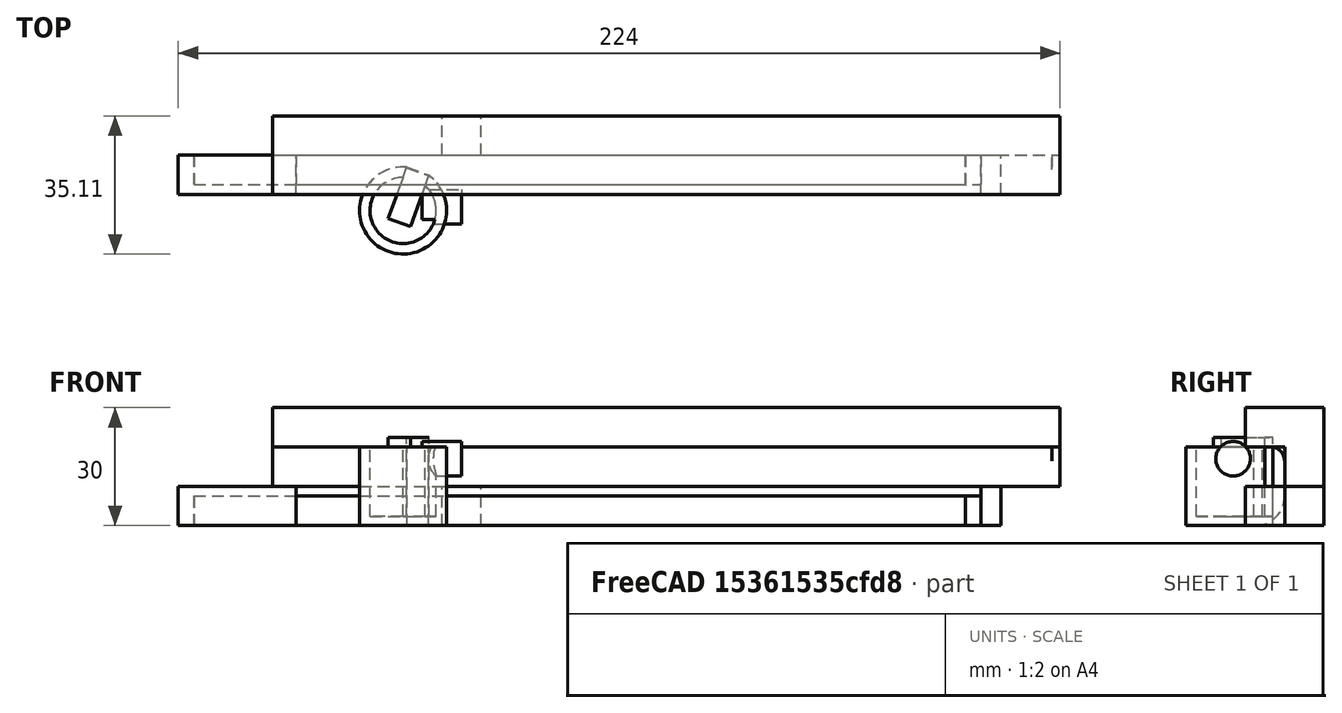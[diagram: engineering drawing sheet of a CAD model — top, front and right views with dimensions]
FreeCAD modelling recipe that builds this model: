
FCSTD DOCUMENT  (FreeCAD 0.19R0.19.2)
Label: v0_76
License: All rights reserved
LicenseURL: http://en.wikipedia.org/wiki/All_rights_reserved
objects: Part::Box×43, Part::Fillet×31, Part::MultiFuse×20, Part::Cut×13, Sketcher::SketchObject×11, Part::Extrusion×9, Part::Cylinder×6, App::MeasureDistance×5, Part::Revolution×1
note: 134 computed .brp shape members not serialized (recipe doc carries the construction recipe); baked Part::Feature solids carry a one-line shape summary decoded from their .brp

FEATURE [Sketcher::SketchObject] Sketch001
  FullyConstrained = true
  sketch-geometry (47):
    g0: Circle CenterX=-129.5 CenterY=-8 CenterZ=0 NormalX=0 NormalY=0 NormalZ=1 AngleXU=0 Radius=1
    g1: Circle CenterX=-129.5 CenterY=-3 CenterZ=0 NormalX=0 NormalY=0 NormalZ=1 AngleXU=0 Radius=1
    g2: Circle CenterX=-124.5 CenterY=-3 CenterZ=0 NormalX=0 NormalY=0 NormalZ=1 AngleXU=0 Radius=1
    g3: BSplineCurve PolesCount=3 KnotsCount=2 Degree=2 IsPeriodic=0
    g4: GeomPoint X=-129.5 Y=-8 Z=0
    g5: GeomPoint X=-124.5 Y=-3 Z=0
    g6: LineSegment StartX=18.6 StartY=-2.9 StartZ=0 EndX=23.6 EndY=-2.9 EndZ=0
    g7: ArcOfCircle CenterX=23.8 CenterY=-14.35 CenterZ=0 NormalX=0 NormalY=0 NormalZ=1 AngleXU=0 Radius=2.3 StartAngle=8e-16 EndAngle=1.5708
    g8: ArcOfCircle CenterX=23.8 CenterY=-18.1 CenterZ=0 NormalX=0 NormalY=0 NormalZ=1 AngleXU=0 Radius=2.3 StartAngle=4.71239 EndAngle=6.28319
    g9: LineSegment StartX=23.8 StartY=-20.4 StartZ=0 EndX=21.1 EndY=-20.4 EndZ=0
    g10: LineSegment StartX=21.1 StartY=-22.9 StartZ=0 EndX=21.1 EndY=-20.4 EndZ=0
    g11: LineSegment StartX=26.1 StartY=-14.35 StartZ=0 EndX=26.1 EndY=-18.1 EndZ=0
    g12: LineSegment StartX=18.6 StartY=-5.40742 StartZ=0 EndX=18.6 EndY=-2.9 EndZ=0
    g13: ArcOfCircle CenterX=18.8 CenterY=-8.1 CenterZ=0 NormalX=0 NormalY=0 NormalZ=1 AngleXU=0 Radius=2.7 StartAngle=1.64494 EndAngle=3.14159
    g14: ArcOfCircle CenterX=18.8 CenterY=-11.85 CenterZ=0 NormalX=0 NormalY=0 NormalZ=1 AngleXU=0 Radius=2.7 StartAngle=3.14159 EndAngle=4.71239
    g15: LineSegment StartX=16.1 StartY=-8.1 StartZ=0 EndX=16.1 EndY=-11.85 EndZ=0
    g16: LineSegment StartX=18.8 StartY=-14.55 StartZ=0 EndX=21.5 EndY=-14.55 EndZ=0
    g17: LineSegment StartX=21.5 StartY=-12.05 StartZ=0 EndX=21.5 EndY=-14.55 EndZ=0
    g18: LineSegment StartX=21.5 StartY=-12.05 StartZ=0 EndX=23.8 EndY=-12.05 EndZ=0
    g19: LineSegment StartX=16.1 StartY=-22.9 StartZ=0 EndX=21.1 EndY=-22.9 EndZ=0
    g20: LineSegment StartX=23.6 StartY=-2.9 StartZ=0 EndX=23.6 EndY=0 EndZ=0
    g21: LineSegment StartX=16.1 StartY=-22.9 StartZ=0 EndX=16.1 EndY=-26.2 EndZ=0
    g22: BSplineCurve PolesCount=3 KnotsCount=2 Degree=2 IsPeriodic=0
    g23: LineSegment StartX=2.6 StartY=-3 StartZ=0 EndX=-124.5 EndY=-3 EndZ=0
    g24: ArcOfCircle CenterX=-134.9 CenterY=-8.6 CenterZ=0 NormalX=0 NormalY=0 NormalZ=1 AngleXU=0 Radius=0.5 StartAngle=4.71238 EndAngle=6.28319
    g25: LineSegment StartX=-141.9 StartY=-9.1 StartZ=0 EndX=-134.9 EndY=-9.1 EndZ=0
    g26: LineSegment StartX=-141.9 StartY=-33.8 StartZ=0 EndX=-141.5 EndY=-33.8 EndZ=0
    g27: LineSegment StartX=-141.9 StartY=-9.1 StartZ=0 EndX=-141.9 EndY=-33.8 EndZ=0
    g28: LineSegment StartX=-134.4 StartY=-8.6 StartZ=0 EndX=-134.4 EndY=0 EndZ=0
    g29: LineSegment StartX=-134.4 StartY=0 StartZ=0 EndX=23.6 EndY=0 EndZ=0
    g30: LineSegment StartX=-133.5 StartY=-26.2 StartZ=0 EndX=16.1 EndY=-26.2 EndZ=0
    g31-g36: Circle x6 (B-spline internal-alignment scaffolding for g37; pole/knot coordinates omitted)
    g37: BSplineCurve PolesCount=6 KnotsCount=4 Degree=3 IsPeriodic=0
    g38-g41: GeomPoint x4 (B-spline internal-alignment scaffolding for g37; pole/knot coordinates omitted)
    g42: BSplineCurve PolesCount=3 KnotsCount=2 Degree=2 IsPeriodic=0
    g43: LineSegment StartX=-129.5 StartY=-8 StartZ=0 EndX=-129.5 EndY=-18.2 EndZ=0
    g44: BSplineCurve PolesCount=3 KnotsCount=2 Degree=2 IsPeriodic=0
    g45: LineSegment StartX=7.6 StartY=-8 StartZ=0 EndX=7.6 EndY=-18.2 EndZ=0
    g46: LineSegment StartX=2.6 StartY=-23.2 StartZ=0 EndX=-124.5 EndY=-23.2 EndZ=0
  constraints (87):
    c: Weight(g0) = 1
    c: Equal(g0,g1)
    c: Equal(g0,g2)
    c: InternalAlignment(g0,g3)
    c: InternalAlignment(g1,g3)
    c: InternalAlignment(g2,g3)
    c: InternalAlignment(g4,g3)
    c: InternalAlignment(g5,g3)
    c: Block(g3)
    c: Block(g8)
    c: Block(g7)
    c: Coincident(g9,g8)
    c: Horizontal(g9)
    c: Vertical(g10)
    c: Coincident(g10,g9)
    c: Coincident(g11,g7)
    c: Coincident(g11,g8)
    c: Vertical(g11)
    c: Vertical(g12)
    c: Block(g12)
    c: Coincident(g6,g12)
    c: Horizontal(g6)
    c: Block(g6)
    c: Coincident(g13,g12)
    c: Block(g14)
    c: Vertical(g15)
    c: Block(g15)
    c: Coincident(g16,g14)
    c: Horizontal(g16)
    c: Vertical(g17)
    c: Coincident(g17,g16)
    c: Block(g17)
    c: Coincident(g18,g7)
    c: Horizontal(g18)
    c: Block(g18)
    c: Coincident(g19,g10)
    c: Horizontal(g19)
    c: Block(g19)
    c: Block(g13)
    c: Coincident(g20,g6)
    c: Vertical(g20)
    c: Vertical(g21)
    c: Block(g21)
    c: Block(g22)
    c: Coincident(g23,g22)
    c: Coincident(g23,g3)
    c: Horizontal(g23)
    c: Block(g24)
    c: Coincident(g25,g24)
    c: Horizontal(g25)
    c: Horizontal(g26)
    c: Block(g26)
    c: Coincident(g27,g25)
    c: Coincident(g27,g26)
    c: Vertical(g27)
    c: Coincident(g28,g24)
    c: Vertical(g28)
    c: Coincident(g29,g28)
    c: Coincident(g29,g20)
    c: Horizontal(g29)
    c: Block(g29)
    c: Block(g25)
    c: Block(g28)
    c: Block(g27)
    c: Coincident(g30,g21)
    c: Horizontal(g30)
    c: Block(g30)
    c: Coincident(g37,g26)
    c: Weight(g31) = 1
    c: Equal(g31, g32-g36) x5
    c: Coincident(g37,g30)
    c: InternalAlignment(g31-g36 -> g37) x6
    c: InternalAlignment(g38-g41 -> g37) x4
    c: Block(g37)
    c: Block(g42)
    c: Coincident(g43,g3)
    c: Coincident(g43,g42)
    c: Vertical(g43)
    c: Distance(g43) = 10.2
    c: Block(g44)
    c: Coincident(g45,g22)
    c: Coincident(g45,g44)
    c: Vertical(g45)
    c: Distance(g45) = 10.2
    c: Coincident(g46,g44)
    c: Coincident(g46,g42)
    c: Horizontal(g46)
FEATURE [Part::Extrusion] Extrude001
  Base = -> Sketch001
  Dir = (0,0,1)
  DirMode = 2
  FaceMakerClass = Part::FaceMakerBullseye
  LengthFwd = 20
  LengthRev = 0
  Solid = true
  Symmetric = false
FEATURE [Sketcher::SketchObject] Sketch004
  FullyConstrained = true
  Placement = pos=(0,0,0) rot=(1,0,0;1.5708rad)
  sketch-geometry (12):
    g0: LineSegment StartX=15.75 StartY=2.5 StartZ=0 EndX=15.75 EndY=0 EndZ=0
    g1: Circle CenterX=15.75 CenterY=2.5 CenterZ=0 NormalX=0 NormalY=0 NormalZ=1 AngleXU=0 Radius=1
    g2: Circle CenterX=10.55 CenterY=2.5 CenterZ=0 NormalX=0 NormalY=0 NormalZ=1 AngleXU=0 Radius=1
    g3: Circle CenterX=10.55 CenterY=8 CenterZ=0 NormalX=0 NormalY=0 NormalZ=1 AngleXU=0 Radius=1
    g4: BSplineCurve PolesCount=3 KnotsCount=2 Degree=2 IsPeriodic=0
    g5: GeomPoint X=15.75 Y=2.5 Z=0
    g6: GeomPoint X=10.55 Y=8 Z=0
    g7: LineSegment StartX=1.9 StartY=8 StartZ=0 EndX=10.55 EndY=8 EndZ=0
    g8: LineSegment StartX=1.9 StartY=-2.4 StartZ=0 EndX=1.9 EndY=8 EndZ=0
    g9: LineSegment StartX=3.30092 StartY=-2.4 StartZ=0 EndX=3.30092 EndY=0 EndZ=0
    g10: LineSegment StartX=15.75 StartY=0 StartZ=0 EndX=3.30092 EndY=0 EndZ=0
    g11: LineSegment StartX=3.30092 StartY=-2.4 StartZ=0 EndX=1.9 EndY=-2.4 EndZ=0
  constraints (26):
    c: Vertical(g0)
    c: Distance(g0) = 2.5
    c: Coincident(g4,g0)
    c: Weight(g1) = 1
    c: Equal(g1,g2)
    c: Equal(g1,g3)
    c: InternalAlignment(g1,g4)
    c: InternalAlignment(g2,g4)
    c: InternalAlignment(g3,g4)
    c: InternalAlignment(g5,g4)
    c: InternalAlignment(g6,g4)
    c: Block(g4)
    c: Coincident(g7,g4)
    c: Horizontal(g7)
    c: Vertical(g8)
    c: Coincident(g8,g7)
    c: Block(g8)
    c: Vertical(g9)
    c: Coincident(g10,g0)
    c: PointOnObject(g10,g-1)
    c: Horizontal(g10)
    c: Coincident(g10,g9)
    c: Block(g9)
    c: Coincident(g11,g9)
    c: Coincident(g11,g8)
    c: Horizontal(g11)
FEATURE [Part::Revolution] Revolve  label="mainScrewStandRevolve"
  Angle = 360
  Axis = (0,0,1)
  Base = (0,0,0)
  FaceMakerClass = Part::FaceMakerBullseye
  Placement = pos=(-101.95,-15.3,0) rot=(0,0,1;0rad)
  Solid = true
  Source = -> Sketch004
  Symmetric = false
FEATURE [Sketcher::SketchObject] Sketch044
  FullyConstrained = true
  MapMode = 4
  Placement = pos=(0,0,0) rot=(0.57735,0.57735,0.57735;2.0944rad)
  sketch-geometry (14):
    g0: LineSegment StartX=6.08745 StartY=-4.11588 StartZ=0 EndX=6.08745 EndY=-2.11589 EndZ=0
    g1: LineSegment StartX=8.08745 StartY=1.38411 StartZ=0 EndX=8.08745 EndY=-1.11589 EndZ=0
    g2: ArcOfCircle CenterX=7.08745 CenterY=-1.11589 CenterZ=0 NormalX=0 NormalY=0 NormalZ=1 AngleXU=0 Radius=1 StartAngle=4.71239 EndAngle=6.28319
    g3: LineSegment StartX=6.08745 StartY=-2.11589 StartZ=0 EndX=7.08745 EndY=-2.11589 EndZ=0
    g4: LineSegment StartX=6.08745 StartY=-4.11588 StartZ=0 EndX=7.08745 EndY=-4.11588 EndZ=0
    g5: ArcOfCircle CenterX=7.08745 CenterY=-1.11589 CenterZ=0 NormalX=0 NormalY=0 NormalZ=1 AngleXU=0 Radius=3 StartAngle=4.71239 EndAngle=6.28319
    g6: ArcOfCircle CenterX=7.08745 CenterY=1.38411 CenterZ=0 NormalX=0 NormalY=0 NormalZ=1 AngleXU=0 Radius=1 StartAngle=5.35e-14 EndAngle=1.5708
    g7: LineSegment StartX=10.0875 StartY=-1.11588 StartZ=0 EndX=10.0875 EndY=1.38411 EndZ=0
    g8: ArcOfCircle CenterX=7.08745 CenterY=1.38411 CenterZ=0 NormalX=0 NormalY=0 NormalZ=1 AngleXU=0 Radius=3 StartAngle=3.57e-14 EndAngle=1.5708
    g9: ArcOfCircle CenterX=4.58745 CenterY=1.38412 CenterZ=0 NormalX=0 NormalY=0 NormalZ=1 AngleXU=0 Radius=1 StartAngle=1.57081 EndAngle=3.14159
    g10: LineSegment StartX=4.58744 StartY=2.38411 StartZ=0 EndX=7.08745 EndY=2.38411 EndZ=0
    g11: LineSegment StartX=4.58745 StartY=4.38411 StartZ=0 EndX=7.08745 EndY=4.38411 EndZ=0
    g12: ArcOfCircle CenterX=4.58745 CenterY=5.38411 CenterZ=0 NormalX=0 NormalY=0 NormalZ=1 AngleXU=0 Radius=1 StartAngle=3.14159 EndAngle=4.71239
    g13: LineSegment StartX=3.58745 StartY=5.38411 StartZ=0 EndX=3.58745 EndY=1.38411 EndZ=0
  constraints (33):
    c: Vertical(g0)
    c: Block(g0)
    c: Block(g1)
    c: Coincident(g2,g1)
    c: Coincident(g3,g0)
    c: Coincident(g3,g2)
    c: Horizontal(g3)
    c: Block(g2)
    c: Coincident(g4,g0)
    c: Horizontal(g4)
    c: Coincident(g5,g2)
    c: Block(g5)
    c: Block(g4)
    c: Coincident(g6,g1)
    c: Block(g6)
    c: Coincident(g7,g5)
    c: Vertical(g7)
    c: Coincident(g8,g6)
    c: Block(g8)
    c: Block(g7)
    c: Coincident(g10,g9)
    c: Coincident(g10,g6)
    c: Horizontal(g10)
    c: Block(g10)
    c: Block(g9)
    c: Coincident(g11,g8)
    c: Horizontal(g11)
    c: Block(g12)
    c: Block(g11)
    c: Coincident(g13,g12)
    c: Coincident(g13,g9)
    c: Vertical(g13)
    c: Tangent(g13,g9)
FEATURE [Sketcher::SketchObject] Sketch045
  FullyConstrained = true
  MapMode = 4
  Placement = pos=(0,0,0) rot=(0.57735,0.57735,0.57735;2.0944rad)
  sketch-geometry (14):
    g0: LineSegment StartX=6.08745 StartY=-4.11588 StartZ=0 EndX=6.08745 EndY=-2.11589 EndZ=0
    g1: LineSegment StartX=8.08745 StartY=1.38411 StartZ=0 EndX=8.08745 EndY=-1.11589 EndZ=0
    g2: ArcOfCircle CenterX=7.08745 CenterY=-1.11589 CenterZ=0 NormalX=0 NormalY=0 NormalZ=1 AngleXU=0 Radius=1 StartAngle=4.71239 EndAngle=6.28319
    g3: LineSegment StartX=6.08745 StartY=-2.11589 StartZ=0 EndX=7.08745 EndY=-2.11589 EndZ=0
    g4: LineSegment StartX=6.08745 StartY=-4.11588 StartZ=0 EndX=7.08745 EndY=-4.11588 EndZ=0
    g5: ArcOfCircle CenterX=7.08745 CenterY=-1.11589 CenterZ=0 NormalX=0 NormalY=0 NormalZ=1 AngleXU=0 Radius=3 StartAngle=4.71239 EndAngle=6.28319
    g6: ArcOfCircle CenterX=7.08745 CenterY=1.38411 CenterZ=0 NormalX=0 NormalY=0 NormalZ=1 AngleXU=0 Radius=1 StartAngle=5.35e-14 EndAngle=1.5708
    g7: LineSegment StartX=10.0875 StartY=-1.11588 StartZ=0 EndX=10.0875 EndY=1.38411 EndZ=0
    g8: ArcOfCircle CenterX=7.08745 CenterY=1.38411 CenterZ=0 NormalX=0 NormalY=0 NormalZ=1 AngleXU=0 Radius=3 StartAngle=3.57e-14 EndAngle=1.5708
    g9: ArcOfCircle CenterX=4.58745 CenterY=1.38412 CenterZ=0 NormalX=0 NormalY=0 NormalZ=1 AngleXU=0 Radius=1 StartAngle=1.57081 EndAngle=3.14159
    g10: LineSegment StartX=4.58744 StartY=2.38411 StartZ=0 EndX=7.08745 EndY=2.38411 EndZ=0
    g11: LineSegment StartX=4.58745 StartY=4.38411 StartZ=0 EndX=7.08745 EndY=4.38411 EndZ=0
    g12: ArcOfCircle CenterX=4.58745 CenterY=5.38411 CenterZ=0 NormalX=0 NormalY=0 NormalZ=1 AngleXU=0 Radius=1 StartAngle=3.14159 EndAngle=4.71239
    g13: LineSegment StartX=3.58745 StartY=5.38411 StartZ=0 EndX=3.58745 EndY=1.38411 EndZ=0
  constraints (33):
    c: Vertical(g0)
    c: Block(g0)
    c: Block(g1)
    c: Coincident(g2,g1)
    c: Coincident(g3,g0)
    c: Coincident(g3,g2)
    c: Horizontal(g3)
    c: Block(g2)
    c: Coincident(g4,g0)
    c: Horizontal(g4)
    c: Coincident(g5,g2)
    c: Block(g5)
    c: Block(g4)
    c: Coincident(g6,g1)
    c: Block(g6)
    c: Coincident(g7,g5)
    c: Vertical(g7)
    c: Coincident(g8,g6)
    c: Block(g8)
    c: Block(g7)
    c: Coincident(g10,g9)
    c: Coincident(g10,g6)
    c: Horizontal(g10)
    c: Block(g10)
    c: Block(g9)
    c: Coincident(g11,g8)
    c: Horizontal(g11)
    c: Block(g12)
    c: Block(g11)
    c: Coincident(g13,g12)
    c: Coincident(g13,g9)
    c: Vertical(g13)
    c: Tangent(g13,g9)
FEATURE [Part::Extrusion] Extrude040
  Base = -> Sketch045
  Dir = (1,0,0)
  DirMode = 2
  FaceMakerClass = Part::FaceMakerBullseye
  LengthFwd = 10
  LengthRev = 0
  Placement = pos=(-71.7,-22.61,4.115) rot=(0,0,1;3.14159rad)
  Solid = true
  Symmetric = false
FEATURE [Part::Box] Box017  label="Cube017"
  AttacherType = Attacher::AttachEngine3D
  Height = 2
  Length = 2
  Placement = pos=(-85.7,-21.3,0) rot=(0,0,1;0rad)
  Width = 2
FEATURE [Part::Box] Box018  label="Cube018"
  AttacherType = Attacher::AttachEngine3D
  Height = 2
  Length = 2
  Placement = pos=(-87.7,-21.3,0) rot=(0,0,1;0rad)
  Width = 2
FEATURE [Part::MultiFuse] Fusion
  Placement = pos=(0,-6.9,0) rot=(0,0,1;0rad)
  Shapes = -> [Box017,Box018]
FEATURE [Part::Box] Box  label="Cube"
  AttacherType = Attacher::AttachEngine3D
  Height = 10
  Length = 10
  Placement = pos=(-107,0,0) rot=(0,0,1;0rad)
  Width = 10
FEATURE [Sketcher::SketchObject] Sketch046
  FullyConstrained = true
  MapMode = 4
  Placement = pos=(0,0,0) rot=(0.57735,0.57735,0.57735;2.0944rad)
  sketch-geometry (14):
    g0: LineSegment StartX=6.08745 StartY=-4.11588 StartZ=0 EndX=6.08745 EndY=-2.11589 EndZ=0
    g1: LineSegment StartX=8.08745 StartY=1.38411 StartZ=0 EndX=8.08745 EndY=-1.11589 EndZ=0
    g2: ArcOfCircle CenterX=7.08745 CenterY=-1.11589 CenterZ=0 NormalX=0 NormalY=0 NormalZ=1 AngleXU=0 Radius=1 StartAngle=4.71239 EndAngle=6.28319
    g3: LineSegment StartX=6.08745 StartY=-2.11589 StartZ=0 EndX=7.08745 EndY=-2.11589 EndZ=0
    g4: LineSegment StartX=6.08745 StartY=-4.11588 StartZ=0 EndX=7.08745 EndY=-4.11588 EndZ=0
    g5: ArcOfCircle CenterX=7.08745 CenterY=-1.11589 CenterZ=0 NormalX=0 NormalY=0 NormalZ=1 AngleXU=0 Radius=3 StartAngle=4.71239 EndAngle=6.28319
    g6: ArcOfCircle CenterX=7.08745 CenterY=1.38411 CenterZ=0 NormalX=0 NormalY=0 NormalZ=1 AngleXU=0 Radius=1 StartAngle=5.35e-14 EndAngle=1.5708
    g7: LineSegment StartX=10.0875 StartY=-1.11588 StartZ=0 EndX=10.0875 EndY=1.38411 EndZ=0
    g8: ArcOfCircle CenterX=7.08745 CenterY=1.38411 CenterZ=0 NormalX=0 NormalY=0 NormalZ=1 AngleXU=0 Radius=3 StartAngle=3.57e-14 EndAngle=1.5708
    g9: ArcOfCircle CenterX=4.58745 CenterY=1.38412 CenterZ=0 NormalX=0 NormalY=0 NormalZ=1 AngleXU=0 Radius=1 StartAngle=1.57081 EndAngle=3.14159
    g10: LineSegment StartX=4.58744 StartY=2.38411 StartZ=0 EndX=7.08745 EndY=2.38411 EndZ=0
    g11: LineSegment StartX=4.58745 StartY=4.38411 StartZ=0 EndX=7.08745 EndY=4.38411 EndZ=0
    g12: ArcOfCircle CenterX=4.58745 CenterY=5.38411 CenterZ=0 NormalX=0 NormalY=0 NormalZ=1 AngleXU=0 Radius=1 StartAngle=3.14159 EndAngle=4.71239
    g13: LineSegment StartX=3.58745 StartY=5.38411 StartZ=0 EndX=3.58745 EndY=1.38411 EndZ=0
  constraints (33):
    c: Vertical(g0)
    c: Block(g0)
    c: Block(g1)
    c: Coincident(g2,g1)
    c: Coincident(g3,g0)
    c: Coincident(g3,g2)
    c: Horizontal(g3)
    c: Block(g2)
    c: Coincident(g4,g0)
    c: Horizontal(g4)
    c: Coincident(g5,g2)
    c: Block(g5)
    c: Block(g4)
    c: Coincident(g6,g1)
    c: Block(g6)
    c: Coincident(g7,g5)
    c: Vertical(g7)
    c: Coincident(g8,g6)
    c: Block(g8)
    c: Block(g7)
    c: Coincident(g10,g9)
    c: Coincident(g10,g6)
    c: Horizontal(g10)
    c: Block(g10)
    c: Block(g9)
    c: Coincident(g11,g8)
    c: Horizontal(g11)
    c: Block(g12)
    c: Block(g11)
    c: Coincident(g13,g12)
    c: Coincident(g13,g9)
    c: Vertical(g13)
    c: Tangent(g13,g9)
FEATURE [Part::Extrusion] Extrude041
  Base = -> Sketch046
  Dir = (1,0,0)
  DirMode = 2
  FaceMakerClass = Part::FaceMakerBullseye
  LengthFwd = 10
  LengthRev = 0
  Placement = pos=(7.5,-22.61,4.115) rot=(0,0,1;3.14159rad)
  Solid = true
  Symmetric = false
FEATURE [Part::Box] Box042  label="Cube042"
  AttacherType = Attacher::AttachEngine3D
  Height = 2
  Length = 2
  Placement = pos=(-87.7,-21.3,0) rot=(0,0,1;0rad)
  Width = 2
FEATURE [Part::Box] Box043  label="Cube043"
  AttacherType = Attacher::AttachEngine3D
  Height = 2
  Length = 2
  Placement = pos=(-85.7,-21.3,0) rot=(0,0,1;0rad)
  Width = 2
FEATURE [Part::MultiFuse] Fusion019
  Placement = pos=(37.15,-6.9,0) rot=(0,0,1;0rad)
  Shapes = -> [Box043,Box042]
FEATURE [Part::Box] Box005  label="Cube005"
  AttacherType = Attacher::AttachEngine3D
  Height = 10
  Length = 198
  Placement = pos=(-30,0,0) rot=(0,0,1;0rad)
  Width = 10
FEATURE [Part::Box] Box004  label="Cube004"
  AttacherType = Attacher::AttachEngine3D
  Height = 10
  Length = 200
  Placement = pos=(-30,0,0) rot=(0,0,1;0rad)
  Width = 10
FEATURE [Part::Fillet] Fillet020
  Base = -> Box004
  Edges = 1 edges r=3.6: [Edge12]
FEATURE [Sketcher::SketchObject] Sketch
  FullyConstrained = true
  sketch-geometry (35):
    g0: Circle CenterX=-101.95 CenterY=-14.3 CenterZ=0 NormalX=0 NormalY=0 NormalZ=1 AngleXU=0 Radius=3.25
    g1: LineSegment StartX=16.1 StartY=-26.2 StartZ=0 EndX=16.1 EndY=-22.9 EndZ=0
    g2: ArcOfCircle CenterX=23.8 CenterY=-14.35 CenterZ=0 NormalX=0 NormalY=0 NormalZ=1 AngleXU=0 Radius=2.3 StartAngle=8e-16 EndAngle=1.5708
    g3: LineSegment StartX=18.6 StartY=-5.40742 StartZ=0 EndX=18.6 EndY=-2.9 EndZ=0
    g4: LineSegment StartX=18.6 StartY=-2.9 StartZ=0 EndX=23.6 EndY=-2.9 EndZ=0
    g5: LineSegment StartX=23.6 StartY=-2.9 StartZ=0 EndX=23.6 EndY=2.58e-14 EndZ=0
    g6: LineSegment StartX=18.8 StartY=-14.55 StartZ=0 EndX=21.5 EndY=-14.55 EndZ=0
    g7: LineSegment StartX=21.5 StartY=-12.05 StartZ=0 EndX=21.5 EndY=-14.55 EndZ=0
    g8: LineSegment StartX=21.5 StartY=-12.05 StartZ=0 EndX=23.8 EndY=-12.05 EndZ=0
    g9: ArcOfCircle CenterX=23.8 CenterY=-18.1 CenterZ=0 NormalX=0 NormalY=0 NormalZ=1 AngleXU=0 Radius=2.3 StartAngle=4.71239 EndAngle=6.28319
    g10: LineSegment StartX=23.8 StartY=-20.4 StartZ=0 EndX=21.1 EndY=-20.4 EndZ=0
    g11: LineSegment StartX=26.1 StartY=-14.35 StartZ=0 EndX=26.1 EndY=-18.1 EndZ=0
    g12: ArcOfCircle CenterX=18.8 CenterY=-8.1 CenterZ=0 NormalX=0 NormalY=0 NormalZ=1 AngleXU=0 Radius=2.7 StartAngle=1.64494 EndAngle=3.14159
    g13: ArcOfCircle CenterX=18.8 CenterY=-11.85 CenterZ=0 NormalX=0 NormalY=0 NormalZ=1 AngleXU=0 Radius=2.7 StartAngle=3.14159 EndAngle=4.71239
    g14: LineSegment StartX=16.1 StartY=-8.1 StartZ=0 EndX=16.1 EndY=-11.85 EndZ=0
    g15: LineSegment StartX=21.1 StartY=-22.9 StartZ=0 EndX=21.1 EndY=-20.4 EndZ=0
    g16: LineSegment StartX=16.1 StartY=-22.9 StartZ=0 EndX=21.1 EndY=-22.9 EndZ=0
    g17: LineSegment StartX=23.6 StartY=2.58e-14 StartZ=0 EndX=-134.4 EndY=2.58e-14 EndZ=0
    g18: LineSegment StartX=-134.4 StartY=2.59e-14 StartZ=0 EndX=-134.4 EndY=-8.6 EndZ=0
    g19: ArcOfCircle CenterX=-134.9 CenterY=-8.6 CenterZ=0 NormalX=0 NormalY=0 NormalZ=1 AngleXU=0 Radius=0.5 StartAngle=4.71238 EndAngle=6.28319
    g20: LineSegment StartX=-134.9 StartY=-9.1 StartZ=0 EndX=-141.9 EndY=-9.1 EndZ=0
    g21: LineSegment StartX=-141.9 StartY=-9.1 StartZ=0 EndX=-141.9 EndY=-33.8 EndZ=0
    g22: LineSegment StartX=-141.9 StartY=-33.8 StartZ=0 EndX=-141.5 EndY=-33.8 EndZ=0
    g23: LineSegment StartX=-133.5 StartY=-26.2 StartZ=0 EndX=16.1 EndY=-26.2 EndZ=0
    g24-g29: Circle x6 (B-spline internal-alignment scaffolding for g30; pole/knot coordinates omitted)
    g30: BSplineCurve PolesCount=6 KnotsCount=4 Degree=3 IsPeriodic=0
    g31-g34: GeomPoint x4 (B-spline internal-alignment scaffolding for g30; pole/knot coordinates omitted)
  constraints (61):
    c: Block(g0)
    c: Vertical(g1)
    c: Distance(g1) = 3.3
    c: Block(g9)
    c: Block(g2)
    c: Coincident(g10,g9)
    c: Horizontal(g10)
    c: Vertical(g15)
    c: Coincident(g15,g10)
    c: Coincident(g11,g2)
    c: Coincident(g11,g9)
    c: Vertical(g11)
    c: Vertical(g3)
    c: Block(g3)
    c: Coincident(g4,g3)
    c: Horizontal(g4)
    c: Vertical(g5)
    c: Block(g5)
    c: Block(g4)
    c: Coincident(g12,g3)
    c: Block(g13)
    c: Coincident(g14,g12)
    c: Vertical(g14)
    c: Block(g14)
    c: Coincident(g6,g13)
    c: Horizontal(g6)
    c: Vertical(g7)
    c: Coincident(g7,g6)
    c: Block(g7)
    c: Coincident(g8,g2)
    c: Horizontal(g8)
    c: Block(g8)
    c: Coincident(g16,g15)
    c: Horizontal(g16)
    c: Block(g16)
    c: Block(g12)
    c: Coincident(g16,g1)
    c: Coincident(g17,g5)
    c: Horizontal(g17)
    c: Vertical(g18)
    c: Horizontal(g20)
    c: Coincident(g19,g18)
    c: Coincident(g19,g20)
    c: Block(g19)
    c: Coincident(g21,g20)
    c: Vertical(g21)
    c: Block(g21)
    c: Coincident(g22,g21)
    c: Horizontal(g22)
    c: Block(g22)
    c: Block(g18)
    c: Coincident(g18,g17)
    c: Coincident(g23,g1)
    c: Horizontal(g23)
    c: Distance(g23) = 149.6
    c: Coincident(g30,g22)
    c: Weight(g24) = 1
    c: Equal(g24, g25-g29) x5
    c: InternalAlignment(g24-g29 -> g30) x6
    c: InternalAlignment(g31-g34 -> g30) x4
    c: Block(g30)
FEATURE [Part::Extrusion] Extrude
  Base = -> Sketch
  Dir = (0,0,1)
  DirMode = 2
  FaceMakerClass = Part::FaceMakerBullseye
  LengthFwd = 2.4
  LengthRev = 0
  Solid = true
  Symmetric = false
FEATURE [Part::Box] Box051  label="Cube051"
  AttacherType = Attacher::AttachEngine3D
  Height = 10
  Length = 198
  Placement = pos=(-30,0,0) rot=(0,0,1;0rad)
  Width = 10
FEATURE [Part::Box] Box052  label="Cube052"
  AttacherType = Attacher::AttachEngine3D
  Height = 5
  Length = 200
  Placement = pos=(-30,6.4,10) rot=(1,0,0;0rad)
  Width = 5
FEATURE [Part::Box] Box053  label="Cube053"
  AttacherType = Attacher::AttachEngine3D
  Height = 5
  Length = 200
  Placement = pos=(-30,6.4,10) rot=(1,0,0;0.872665rad)
  Width = 5
FEATURE [Part::Box] Box054  label="Cube054"
  AttacherType = Attacher::AttachEngine3D
  Height = 10
  Length = 200
  Placement = pos=(-30,0,0) rot=(0,0,1;0rad)
  Width = 10
FEATURE [Part::Fillet] Fillet021
  Base = -> Box054
  Edges = 1 edges r=3.6: [Edge12]
FEATURE [Part::Cut] Cut015
  Base = -> Box051
  Tool = -> Fillet021
FEATURE [Part::MultiFuse] Fusion033  label="removeFromMainFusion014"
  Placement = pos=(-120,-10,10) rot=(0,0,1;0rad)
  Shapes = -> [Box053,Box052,Cut015]
FEATURE [Part::Box] Box055  label="Cube055"
  AttacherType = Attacher::AttachEngine3D
  Height = 10
  Length = 190
  Placement = pos=(-30,0,0) rot=(0,0,1;0rad)
  Width = 10
FEATURE [Part::Box] Box056  label="Cube056"
  AttacherType = Attacher::AttachEngine3D
  Height = 10
  Length = 190
  Placement = pos=(-35,0,0) rot=(0,0,1;0rad)
  Width = 10
FEATURE [Part::Fillet] Fillet022
  Base = -> Box055
  Edges = 1 edges r=7.5: [Edge11]
FEATURE [Part::Cut] Cut014  label="filletMain001"
  Base = -> Box056
  Placement = pos=(-120,-10,0) rot=(0,0,1;0rad)
  Tool = -> Fillet022
FEATURE [Part::MultiFuse] Fusion032  label="removeFromMain001"
  Shapes = -> [Fusion033,Cut014]
FEATURE [Part::Cut] Cut017
  Base = -> Extrude
  Tool = -> Fusion032
FEATURE [Part::Box] Box063  label="Cube063"
  AttacherType = Attacher::AttachEngine3D
  Height = 10
  Length = 198
  Placement = pos=(-30,0,0) rot=(0,0,1;0rad)
  Width = 10
FEATURE [Part::Box] Box064  label="Cube064"
  AttacherType = Attacher::AttachEngine3D
  Height = 5
  Length = 200
  Placement = pos=(-30,6.4,10) rot=(1,0,0;0rad)
  Width = 5
FEATURE [Part::Box] Box065  label="Cube065"
  AttacherType = Attacher::AttachEngine3D
  Height = 5
  Length = 200
  Placement = pos=(-30,6.4,10) rot=(1,0,0;0.872665rad)
  Width = 5
FEATURE [Part::Box] Box066  label="Cube066"
  AttacherType = Attacher::AttachEngine3D
  Height = 10
  Length = 200
  Placement = pos=(-30,0,0) rot=(0,0,1;0rad)
  Width = 10
FEATURE [Part::Fillet] Fillet023
  Base = -> Box066
  Edges = 1 edges r=3.6: [Edge12]
FEATURE [Part::Cut] Cut018
  Base = -> Box063
  Tool = -> Fillet023
FEATURE [Part::MultiFuse] Fusion035  label="removeFromMainFusion015"
  Placement = pos=(-120,-10,10) rot=(0,0,1;0rad)
  Shapes = -> [Box065,Box064,Cut018]
FEATURE [Part::Box] Box067  label="Cube067"
  AttacherType = Attacher::AttachEngine3D
  Height = 10
  Length = 190
  Placement = pos=(-30,0,0) rot=(0,0,1;0rad)
  Width = 10
FEATURE [Part::Fillet] Fillet024
  Base = -> Box067
  Edges = 1 edges r=7.5: [Edge11]
FEATURE [Part::Box] Box068  label="Cube068"
  AttacherType = Attacher::AttachEngine3D
  Height = 10
  Length = 190
  Placement = pos=(-35,0,0) rot=(0,0,1;0rad)
  Width = 10
FEATURE [Part::Cut] Cut019  label="filletMain002"
  Base = -> Box068
  Placement = pos=(-120,-10,0) rot=(0,0,1;0rad)
  Tool = -> Fillet024
FEATURE [Part::MultiFuse] Fusion036  label="removeFromMain002"
  Shapes = -> [Fusion035,Cut019]
FEATURE [Part::Box] Box069  label="Cube069"
  AttacherType = Attacher::AttachEngine3D
  Height = 20
  Length = 10
  Placement = pos=(-144.4,-8,0) rot=(0,0,1;0rad)
  Width = 10
FEATURE [Part::Box] Box070  label="Cube070"
  AttacherType = Attacher::AttachEngine3D
  Height = 20
  Length = 30
  Placement = pos=(-120,0,0) rot=(0,0,1;0rad)
  Width = 20
FEATURE [Part::MultiFuse] Fusion037  label="removeFromIntegrityIncreaserFusion037"
  Shapes = -> [Box069,Box070,Fusion036]
FEATURE [Sketcher::SketchObject] Sketch047
  FullyConstrained = true
  sketch-geometry (4):
    g0: LineSegment StartX=20.5 StartY=-1.82002 StartZ=0 EndX=20.5 EndY=-36 EndZ=0
    g1: LineSegment StartX=32.7 StartY=-36 StartZ=0 EndX=32.7 EndY=-1.82002 EndZ=0
    g2: LineSegment StartX=20.5 StartY=-1.82002 StartZ=0 EndX=32.7 EndY=-1.82002 EndZ=0
    g3: LineSegment StartX=20.5 StartY=-36 StartZ=0 EndX=32.7 EndY=-36 EndZ=0
  constraints (12):
    c: Vertical(g0)
    c: Distance(g0) = 34.18
    c: Vertical(g1)
    c: Block(g0)
    c: Coincident(g2,g0)
    c: Horizontal(g2)
    c: Coincident(g2,g1)
    c: Block(g2)
    c: Block(g1)
    c: Coincident(g3,g0)
    c: Coincident(g3,g1)
    c: Horizontal(g3)
FEATURE [Part::Cut] Cut021
  Base = -> Box005
  Tool = -> Fillet020
FEATURE [Part::Box] Box073  label="Cube073"
  AttacherType = Attacher::AttachEngine3D
  Height = 10
  Length = 200
  Placement = pos=(-30,10,0) rot=(0,0,1;0rad)
  Width = 10
FEATURE [Part::Box] Box074  label="Cube074"
  AttacherType = Attacher::AttachEngine3D
  Height = 10
  Length = 200
  Placement = pos=(-30,0,10) rot=(0,0,1;0rad)
  Width = 10
FEATURE [Part::Box] Box075  label="Cube075"
  AttacherType = Attacher::AttachEngine3D
  Height = 10
  Length = 200
  Placement = pos=(-30,10,10) rot=(0,0,1;0rad)
  Width = 10
FEATURE [Part::MultiFuse] Fusion043  label="removeFromMainFusion043"
  Placement = pos=(-120,-10,10) rot=(0,0,1;0rad)
  Shapes = -> [Cut021,Box074,Box073,Box075]
FEATURE [Part::Box] Box076  label="Cube076"
  AttacherType = Attacher::AttachEngine3D
  Height = 10
  Length = 200
  Placement = pos=(-160,0,0) rot=(0,0,1;0rad)
  Width = 10
FEATURE [Part::Box] Box077  label="Cube077"
  AttacherType = Attacher::AttachEngine3D
  Height = 10
  Length = 170
  Placement = pos=(-130,0,0) rot=(0,0,1;0rad)
  Width = 10
FEATURE [Part::Fillet] Fillet028
  Base = -> Box077
  Edges = 1 edges r=7.5: [Edge11]
FEATURE [Part::Cut] Cut024
  Base = -> Box076
  Placement = pos=(-14,-10,0) rot=(0,0,1;0rad)
  Tool = -> Fillet028
FEATURE [Part::Box] Box078  label="Cube078"
  AttacherType = Attacher::AttachEngine3D
  Height = 10
  Length = 200
  Width = 10
FEATURE [Part::Box] Box079  label="Cube079"
  AttacherType = Attacher::AttachEngine3D
  Height = 10
  Length = 205
  Placement = pos=(10,0,0) rot=(0,0,1;0rad)
  Width = 10
FEATURE [Part::Fillet] Fillet029
  Base = -> Box078
  Edges = 1 edges r=7.5: [Edge11]
  Placement = pos=(10,0,0) rot=(0,0,1;0rad)
FEATURE [Part::Cut] Cut025  label="removeFromMainCut025"
  Base = -> Box079
  Placement = pos=(-180,-10,0) rot=(0,0,1;0rad)
  Tool = -> Fillet029
FEATURE [Part::Cylinder] Cylinder001
  Angle = 360
  AttacherType = Attacher::AttachEngine3D
  Height = 10
  Placement = pos=(-36.2,-2,12) rot=(0,1,0;1.5708rad)
  Radius = 2
FEATURE [App::MeasureDistance] Distance  label="Distance: 4.02 mm"
  Distance = 4.02
  P1 = (-33.21,5.8978,9.90268)
  P2 = (-29.19,5.8978,9.90268)
FEATURE [Part::Fillet] Fillet030
  Base = -> Cylinder001
  Edges = 1 edges r=1.8: [Edge3]
FEATURE [Part::Fillet] Fillet031
  Base = -> Fillet030
  Edges = 1 edges r=1.8: [Edge2]
FEATURE [Part::Cylinder] Cylinder003
  Angle = 360
  AttacherType = Attacher::AttachEngine3D
  Height = 10
  Placement = pos=(-36.2,-2,12) rot=(0,1,0;1.5708rad)
  Radius = 2
FEATURE [Part::Fillet] Fillet035
  Base = -> Cylinder003
  Edges = 1 edges r=1.8: [Edge3]
FEATURE [Part::Fillet] Fillet036
  Base = -> Fillet035
  Edges = 1 edges r=1.8: [Edge2]
  Placement = pos=(-12.8,0,0) rot=(0,0,1;0rad)
FEATURE [Part::Cylinder] Cylinder004
  Angle = 360
  AttacherType = Attacher::AttachEngine3D
  Height = 10
  Placement = pos=(-36.2,-2,12) rot=(0,1,0;1.5708rad)
  Radius = 2
FEATURE [Part::Fillet] Fillet038
  Base = -> Cylinder004
  Edges = 1 edges r=1.8: [Edge3]
FEATURE [Part::Fillet] Fillet037
  Base = -> Fillet038
  Edges = 1 edges r=1.8: [Edge2]
  Placement = pos=(-6.4,0,0) rot=(0,0,1;0rad)
FEATURE [Sketcher::SketchObject] Sketch048
  FullyConstrained = true
  sketch-geometry (4):
    g0: LineSegment StartX=-5.1 StartY=-34.18 StartZ=0 EndX=5.1 EndY=-34.18 EndZ=0
    g1: LineSegment StartX=-5.1 StartY=-3.93167e-07 StartZ=0 EndX=-5.1 EndY=-34.18 EndZ=0
    g2: LineSegment StartX=5.1 StartY=-34.18 StartZ=0 EndX=5.1 EndY=-3.93167e-07 EndZ=0
    g3: LineSegment StartX=-5.1 StartY=-3.93167e-07 StartZ=0 EndX=5.1 EndY=-3.93167e-07 EndZ=0
  constraints (10):
    c: Horizontal(g0)
    c: Block(g0)
    c: Coincident(g1,g0)
    c: Vertical(g1)
    c: Coincident(g2,g0)
    c: Vertical(g2)
    c: Coincident(g3,g1)
    c: Coincident(g3,g2)
    c: Horizontal(g3)
    c: Block(g3)
FEATURE [Part::Extrusion] Extrude044
  Base = -> Sketch048
  Dir = (0,0,1)
  DirMode = 2
  FaceMakerClass = Part::FaceMakerBullseye
  LengthFwd = 6.2
  LengthRev = 0
  Solid = true
  Symmetric = false
FEATURE [Part::Fillet] Fillet039
  Base = -> Extrude044
  Edges = 1 edges r=3.09: [Edge7]
FEATURE [Part::Fillet] Fillet040
  Base = -> Fillet039
  Edges = 1 edges r=3.09: [Edge8]
FEATURE [Part::Fillet] Fillet041
  Base = -> Fillet040
  Edges = 1 edges r=3.09: [Edge17]
FEATURE [Part::Fillet] Fillet042  label="removeFromMainToMakeUSBCableHole"
  Base = -> Fillet041
  Edges = 1 edges r=3.09: [Edge10]
  Placement = pos=(-111.4,30,10.9) rot=(0,1,0;1.5708rad)
FEATURE [Part::Cylinder] Cylinder
  Angle = 360
  AttacherType = Attacher::AttachEngine3D
  Height = 17.6
  Placement = pos=(-116.86,-14.05,2.4) rot=(0,0,1;0rad)
  Radius = 8.4
FEATURE [Part::Box] Box080  label="Cube080"
  AttacherType = Attacher::AttachEngine3D
  Height = 20
  Length = 6
  Placement = pos=(-120.65,-16.05,2.4) rot=(0,0,-1;0.349066rad)
  Width = 13.85
FEATURE [Part::Cylinder] Cylinder005
  Angle = 360
  AttacherType = Attacher::AttachEngine3D
  Height = 20
  Placement = pos=(-116.86,-14.05,30) rot=(0,0,1;0rad)
  Radius = 11.06
FEATURE [Part::Box] Box081  label="Cube081"
  AttacherType = Attacher::AttachEngine3D
  Height = 20
  Length = 10
  Placement = pos=(-115.9,-3.3,30) rot=(0,0,-1;0.314159rad)
  Width = 10
FEATURE [App::MeasureDistance] Distance001  label="Distance: 2.40 mm"
  Distance = 2.4
  P1 = (-129.5,-19.3,2.4)
  P2 = (-129.5,-19.3,0)
FEATURE [Part::MultiFuse] Fusion047
  Shapes = -> [Box080,Cylinder]
FEATURE [Part::Cylinder] Cylinder006
  Angle = 360
  AttacherType = Attacher::AttachEngine3D
  Height = 10
  Placement = pos=(-112,-13.1,17) rot=(0,1,0;1.5708rad)
  Radius = 4.4
FEATURE [Part::MultiFuse] Fusion048  label="removeFromMainToCreateHoleForUSBCablePillar"
  Shapes = -> [Fusion047,Cylinder006]
FEATURE [Part::Extrusion] Extrude046
  Base = -> Sketch047
  Dir = (0,0,1)
  DirMode = 2
  FaceMakerClass = Part::FaceMakerBullseye
  LengthFwd = 8
  LengthRev = 0
  Solid = true
  Symmetric = false
FEATURE [App::MeasureDistance] Distance002  label="Distance: 12.20 mm"
  Distance = 12.2
  P1 = (32.7,-36,8)
  P2 = (20.5,-36,8)
FEATURE [Part::Fillet] Fillet
  Base = -> Extrude046
  Edges = 1 edges r=3.9: [Edge12]
FEATURE [Part::Fillet] Fillet048
  Base = -> Fillet
  Edges = 1 edges r=3.9: [Edge8]
FEATURE [Part::Fillet] Fillet049
  Base = -> Fillet048
  Edges = 1 edges r=3.9: [Edge17]
FEATURE [Part::Fillet] Fillet050
  Base = -> Fillet049
  Edges = 1 edges r=3.9: [Edge11]
  Placement = pos=(-55,0,8.3) rot=(1,0,0;0.191986rad)
FEATURE [Part::MultiFuse] Fusion049
  Shapes = -> [Fillet031,Fillet036,Fillet037]
FEATURE [Part::Cut] Cut027
  Base = -> Cylinder005
  Placement = pos=(0,0,-30) rot=(0,0,1;0rad)
  Tool = -> Box081
FEATURE [Sketcher::SketchObject] Sketch049
  FullyConstrained = true
  sketch-geometry (4):
    g0: LineSegment StartX=-5.1 StartY=-34.18 StartZ=0 EndX=5.1 EndY=-34.18 EndZ=0
    g1: LineSegment StartX=-5.1 StartY=-3.93167e-07 StartZ=0 EndX=-5.1 EndY=-34.18 EndZ=0
    g2: LineSegment StartX=5.1 StartY=-34.18 StartZ=0 EndX=5.1 EndY=-3.93167e-07 EndZ=0
    g3: LineSegment StartX=-5.1 StartY=-3.93167e-07 StartZ=0 EndX=5.1 EndY=-3.93167e-07 EndZ=0
  constraints (10):
    c: Horizontal(g0)
    c: Block(g0)
    c: Coincident(g1,g0)
    c: Vertical(g1)
    c: Coincident(g2,g0)
    c: Vertical(g2)
    c: Coincident(g3,g1)
    c: Coincident(g3,g2)
    c: Horizontal(g3)
    c: Block(g3)
FEATURE [Part::Extrusion] Extrude047
  Base = -> Sketch049
  Dir = (0,0,1)
  DirMode = 2
  FaceMakerClass = Part::FaceMakerBullseye
  LengthFwd = 6.2
  LengthRev = 0
  Solid = true
  Symmetric = false
FEATURE [Part::Fillet] Fillet054
  Base = -> Extrude047
  Edges = 1 edges r=3.09: [Edge7]
FEATURE [Part::Fillet] Fillet051
  Base = -> Fillet054
  Edges = 1 edges r=3.09: [Edge8]
FEATURE [Part::Fillet] Fillet052
  Base = -> Fillet051
  Edges = 1 edges r=3.09: [Edge17]
FEATURE [Part::Fillet] Fillet053  label="removeFromMainToMakeUSBCableHole001"
  Base = -> Fillet052
  Edges = 1 edges r=3.09: [Edge10]
  Placement = pos=(-111.4,30,14.9) rot=(0,1,0;1.5708rad)
FEATURE [Sketcher::SketchObject] Sketch050
  FullyConstrained = true
  sketch-geometry (4):
    g0: LineSegment StartX=-5.1 StartY=-34.18 StartZ=0 EndX=5.1 EndY=-34.18 EndZ=0
    g1: LineSegment StartX=-5.1 StartY=-3.93167e-07 StartZ=0 EndX=-5.1 EndY=-34.18 EndZ=0
    g2: LineSegment StartX=5.1 StartY=-34.18 StartZ=0 EndX=5.1 EndY=-3.93167e-07 EndZ=0
    g3: LineSegment StartX=-5.1 StartY=-3.93167e-07 StartZ=0 EndX=5.1 EndY=-3.93167e-07 EndZ=0
  constraints (10):
    c: Horizontal(g0)
    c: Block(g0)
    c: Coincident(g1,g0)
    c: Vertical(g1)
    c: Coincident(g2,g0)
    c: Vertical(g2)
    c: Coincident(g3,g1)
    c: Coincident(g3,g2)
    c: Horizontal(g3)
    c: Block(g3)
FEATURE [Part::Extrusion] Extrude048
  Base = -> Sketch050
  Dir = (0,0,1)
  DirMode = 2
  FaceMakerClass = Part::FaceMakerBullseye
  LengthFwd = 6.2
  LengthRev = 0
  Solid = true
  Symmetric = false
FEATURE [Part::Fillet] Fillet058
  Base = -> Extrude048
  Edges = 1 edges r=3.09: [Edge7]
FEATURE [Part::Fillet] Fillet056
  Base = -> Fillet058
  Edges = 1 edges r=3.09: [Edge8]
FEATURE [Part::Fillet] Fillet055
  Base = -> Fillet056
  Edges = 1 edges r=3.09: [Edge17]
FEATURE [Part::Fillet] Fillet057  label="removeFromMainToMakeUSBCableHole002"
  Base = -> Fillet055
  Edges = 1 edges r=3.09: [Edge10]
  Placement = pos=(-111.4,30,18.4) rot=(0,1,0;1.5708rad)
FEATURE [Part::MultiFuse] Fusion050  label="removeFusion050"
  Shapes = -> [Fillet057,Fillet053,Fillet042]
FEATURE [Part::Box] Box082  label="Cube082"
  AttacherType = Attacher::AttachEngine3D
  Height = 3
  Length = 3
  Placement = pos=(-20,-23.5,17) rot=(0,0,1;0rad)
  Width = 23
FEATURE [Part::Box] Box083  label="Cube083"
  AttacherType = Attacher::AttachEngine3D
  Height = 3
  Length = 3
  Placement = pos=(-40,-23.5,17) rot=(0,0,1;0rad)
  Width = 23
FEATURE [Part::Box] Box086  label="Cube086"
  AttacherType = Attacher::AttachEngine3D
  Height = 8
  Length = 28
  Placement = pos=(-132,-26,0) rot=(0,0,1;0rad)
  Width = 23
FEATURE [Part::Box] Box087  label="Cube087"
  AttacherType = Attacher::AttachEngine3D
  Height = 8
  Length = 12
  Placement = pos=(-98,-26,0) rot=(0,0,1;0rad)
  Width = 23
FEATURE [Part::Box] Box088  label="Cube088"
  AttacherType = Attacher::AttachEngine3D
  Height = 8
  Length = 12
  Placement = pos=(-108,-10,0) rot=(0,0,1;0rad)
  Width = 8
FEATURE [Part::MultiFuse] Fusion051  label="extraStrengthFusion051"
  Shapes = -> [Box087,Box088,Box086]
FEATURE [Part::Fillet] Fillet059
  Base = -> Fusion051
  Edges = 1 edges r=4: [Edge8]
FEATURE [Part::MultiFuse] Fusion052  label="main"
  Shapes = -> [Box083,Box082,Cut017,Extrude001,Fillet059,Revolve]
FEATURE [Part::Cut] Cut028
  Base = -> Fusion052
  Tool = -> Fusion050
FEATURE [Part::Fillet] Fillet060
  Base = -> Cut028
  Edges = 1 edges r=2: [Edge287]
FEATURE [Part::Cut] Cut029
  Base = -> Fillet060
  Tool = -> Fillet050
FEATURE [Part::Cut] Cut030
  Base = -> Cut029
  Tool = -> Fusion049
FEATURE [Part::Cut] Cut031  label="mainCut031"
  Base = -> Cut030
  Tool = -> Fusion037
FEATURE [App::MeasureDistance] Distance003  label="Distance: 69.20 mm"
  Distance = 69.2
  P1 = (-2.5,-29.6975,8.49911)
  P2 = (-71.7,-29.6975,8.49911)
FEATURE [App::MeasureDistance] Distance004  label="Distance: 10.00 mm"
  Distance = 10
  P1 = (-56.7,-29.6975,8.49911)
  P2 = (-46.7,-29.6975,8.49911)
FEATURE [Sketcher::SketchObject] Sketch051
  FullyConstrained = true
  MapMode = 4
  Placement = pos=(0,0,0) rot=(0.57735,0.57735,0.57735;2.0944rad)
  sketch-geometry (14):
    g0: LineSegment StartX=6.08745 StartY=-4.11588 StartZ=0 EndX=6.08745 EndY=-2.11589 EndZ=0
    g1: LineSegment StartX=8.08745 StartY=1.38411 StartZ=0 EndX=8.08745 EndY=-1.11589 EndZ=0
    g2: ArcOfCircle CenterX=7.08745 CenterY=-1.11589 CenterZ=0 NormalX=0 NormalY=0 NormalZ=1 AngleXU=0 Radius=1 StartAngle=4.71239 EndAngle=6.28319
    g3: LineSegment StartX=6.08745 StartY=-2.11589 StartZ=0 EndX=7.08745 EndY=-2.11589 EndZ=0
    g4: LineSegment StartX=6.08745 StartY=-4.11588 StartZ=0 EndX=7.08745 EndY=-4.11588 EndZ=0
    g5: ArcOfCircle CenterX=7.08745 CenterY=-1.11589 CenterZ=0 NormalX=0 NormalY=0 NormalZ=1 AngleXU=0 Radius=3 StartAngle=4.71239 EndAngle=6.28319
    g6: ArcOfCircle CenterX=7.08745 CenterY=1.38411 CenterZ=0 NormalX=0 NormalY=0 NormalZ=1 AngleXU=0 Radius=1 StartAngle=5.35e-14 EndAngle=1.5708
    g7: LineSegment StartX=10.0875 StartY=-1.11588 StartZ=0 EndX=10.0875 EndY=1.38411 EndZ=0
    g8: ArcOfCircle CenterX=7.08745 CenterY=1.38411 CenterZ=0 NormalX=0 NormalY=0 NormalZ=1 AngleXU=0 Radius=3 StartAngle=3.57e-14 EndAngle=1.5708
    g9: ArcOfCircle CenterX=4.58745 CenterY=1.38412 CenterZ=0 NormalX=0 NormalY=0 NormalZ=1 AngleXU=0 Radius=1 StartAngle=1.57081 EndAngle=3.14159
    g10: LineSegment StartX=4.58744 StartY=2.38411 StartZ=0 EndX=7.08745 EndY=2.38411 EndZ=0
    g11: LineSegment StartX=4.58745 StartY=4.38411 StartZ=0 EndX=7.08745 EndY=4.38411 EndZ=0
    g12: ArcOfCircle CenterX=4.58745 CenterY=5.38411 CenterZ=0 NormalX=0 NormalY=0 NormalZ=1 AngleXU=0 Radius=1 StartAngle=3.14159 EndAngle=4.71239
    g13: LineSegment StartX=3.58745 StartY=5.38411 StartZ=0 EndX=3.58745 EndY=1.38411 EndZ=0
  constraints (33):
    c: Vertical(g0)
    c: Block(g0)
    c: Block(g1)
    c: Coincident(g2,g1)
    c: Coincident(g3,g0)
    c: Coincident(g3,g2)
    c: Horizontal(g3)
    c: Block(g2)
    c: Coincident(g4,g0)
    c: Horizontal(g4)
    c: Coincident(g5,g2)
    c: Block(g5)
    c: Block(g4)
    c: Coincident(g6,g1)
    c: Block(g6)
    c: Coincident(g7,g5)
    c: Vertical(g7)
    c: Coincident(g8,g6)
    c: Block(g8)
    c: Block(g7)
    c: Coincident(g10,g9)
    c: Coincident(g10,g6)
    c: Horizontal(g10)
    c: Block(g10)
    c: Block(g9)
    c: Coincident(g11,g8)
    c: Horizontal(g11)
    c: Block(g12)
    c: Block(g11)
    c: Coincident(g13,g12)
    c: Coincident(g13,g9)
    c: Vertical(g13)
    c: Tangent(g13,g9)
FEATURE [Part::Extrusion] Extrude049
  Base = -> Sketch051
  Dir = (1,0,0)
  DirMode = 2
  FaceMakerClass = Part::FaceMakerBullseye
  LengthFwd = 10
  LengthRev = 0
  Placement = pos=(-34.55,-22.61,4.115) rot=(0,0,1;3.14159rad)
  Solid = true
  Symmetric = false
FEATURE [Part::Box] Box089  label="Cube089"
  AttacherType = Attacher::AttachEngine3D
  Height = 2
  Length = 2
  Placement = pos=(-87.7,-21.3,0) rot=(0,0,1;0rad)
  Width = 2
FEATURE [Part::Box] Box090  label="Cube090"
  AttacherType = Attacher::AttachEngine3D
  Height = 2
  Length = 2
  Placement = pos=(-85.7,-21.3,0) rot=(0,0,1;0rad)
  Width = 2
FEATURE [Part::MultiFuse] Fusion053
  Placement = pos=(55.15,-6.9,0) rot=(0,0,1;0rad)
  Shapes = -> [Box090,Box089]
FEATURE [Part::Box] Box091  label="Cube091"
  AttacherType = Attacher::AttachEngine3D
  Height = 2
  Length = 2
  Placement = pos=(-87.7,-21.3,0) rot=(0,0,1;0rad)
  Width = 2
FEATURE [Part::Box] Box092  label="Cube092"
  AttacherType = Attacher::AttachEngine3D
  Height = 2
  Length = 2
  Placement = pos=(-85.7,-21.3,0) rot=(0,0,1;0rad)
  Width = 2
FEATURE [Part::MultiFuse] Fusion054
  Placement = pos=(79.2,-6.9,0) rot=(0,0,1;0rad)
  Shapes = -> [Box092,Box091]
FEATURE [Part::Box] Box093  label="Cube093"
  AttacherType = Attacher::AttachEngine3D
  Height = 2
  Length = 2
  Placement = pos=(-87.7,-21.3,0) rot=(0,0,1;0rad)
  Width = 2
FEATURE [Part::Box] Box094  label="Cube094"
  AttacherType = Attacher::AttachEngine3D
  Height = 2
  Length = 2
  Placement = pos=(-85.7,-21.3,0) rot=(0,0,1;0rad)
  Width = 2
FEATURE [Part::MultiFuse] Fusion055
  Placement = pos=(97.2,-6.9,0) rot=(0,0,1;0rad)
  Shapes = -> [Box094,Box093]
FEATURE [Part::Box] Box095  label="Cube095"
  AttacherType = Attacher::AttachEngine3D
  Height = 2
  Length = 2
  Placement = pos=(-87.7,-21.3,0) rot=(0,0,1;0rad)
  Width = 2
FEATURE [Part::Box] Box096  label="Cube096"
  AttacherType = Attacher::AttachEngine3D
  Height = 2
  Length = 2
  Placement = pos=(-85.7,-21.3,0) rot=(0,0,1;0rad)
  Width = 2
FEATURE [Part::MultiFuse] Fusion056
  Placement = pos=(18,-6.9,0) rot=(0,0,1;0rad)
  Shapes = -> [Box096,Box095]
FEATURE [Part::MultiFuse] Fusion057
  Shapes = -> [Fusion056,Fusion055,Extrude041,Fusion054,Fusion053,Extrude049,Fusion019,Extrude040,Fusion]
FEATURE [Part::MultiFuse] Fusion058
  Shapes = -> [Fusion057,Cut031]
